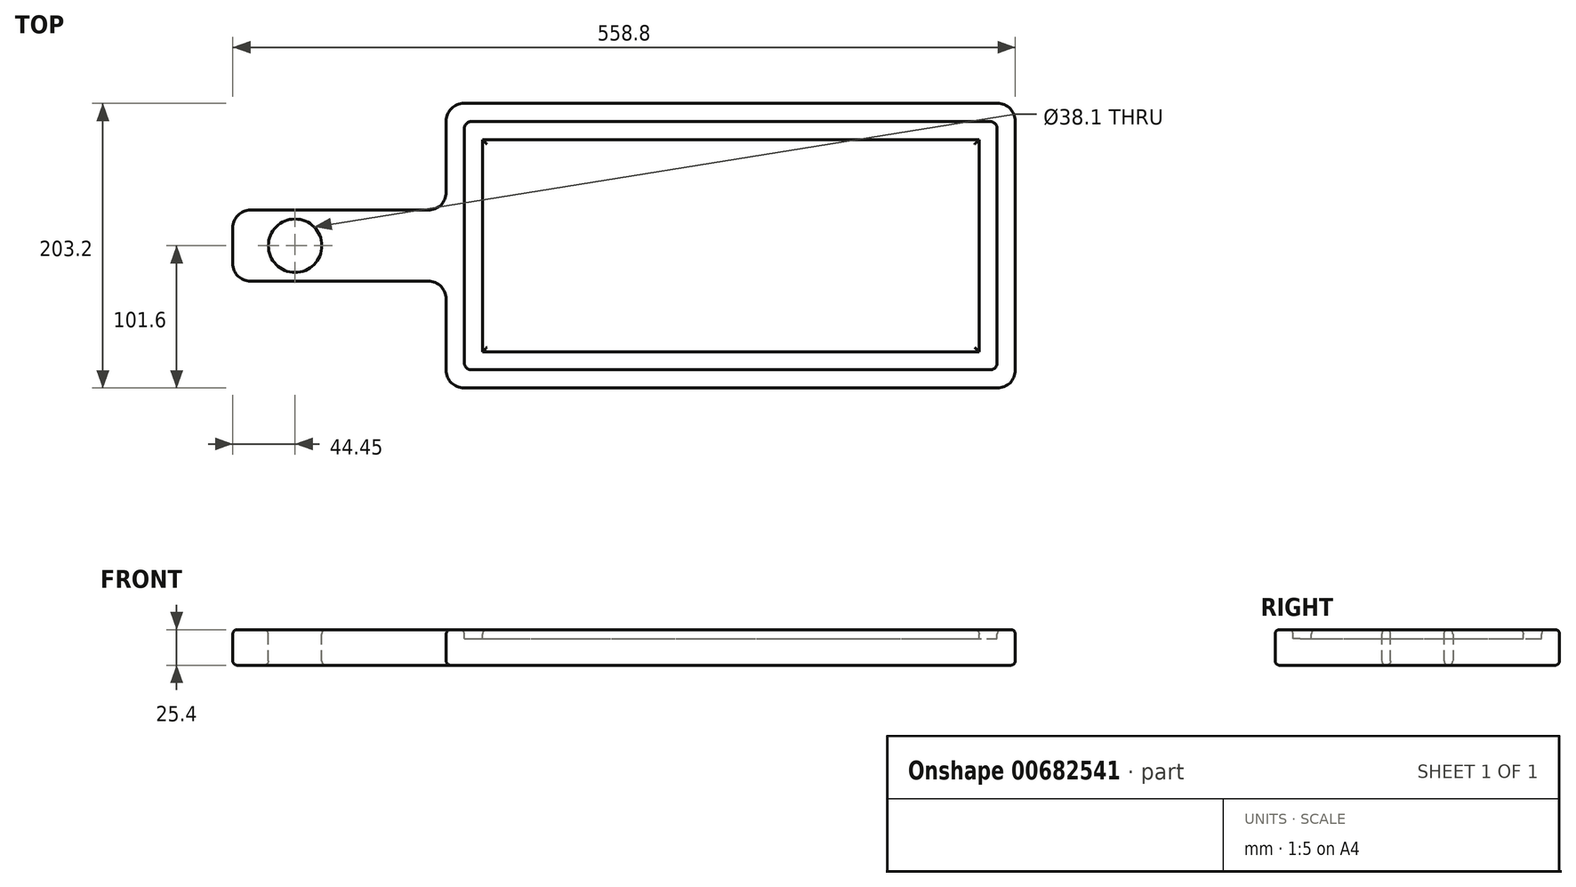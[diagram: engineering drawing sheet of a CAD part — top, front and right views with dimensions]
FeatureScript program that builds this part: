
annotation { "Feature Type Name" : "Feature", "Feature Type Description" : "" }
export const myFeature = defineFeature(function(context is Context, id is Id, definition is map)
    precondition{}
    {
        {
            var Q0;
            Q0=qCreatedBy(makeId("Top.planeOp"),FACE);
            var sketch = newSketch(context, id + "F0", { "sketchPlane" : qUnion([Q0])});
            skLineSegment(sketch, "E0.bottom", {"start": v(0, 0) * mm, "end": v(406.4, 0) * mm});
            skLineSegment(sketch, "E0.top", {"start": v(0, 203.2) * mm, "end": v(406.4, 203.2) * mm});
            skLineSegment(sketch, "E0.left", {"start": v(0, 0) * mm, "end": v(0, 203.2) * mm});
            skLineSegment(sketch, "E0.right", {"start": v(406.4, 0) * mm, "end": v(406.4, 203.2) * mm});
            skLineSegment(sketch, "E1.bottom", {"start": v(0, 127) * mm, "end": v(-152.4, 127) * mm});
            skLineSegment(sketch, "E1.top", {"start": v(0, 76.2) * mm, "end": v(-152.4, 76.2) * mm});
            skLineSegment(sketch, "E1.left", {"start": v(0, 127) * mm, "end": v(0, 76.2) * mm});
            skLineSegment(sketch, "E1.right", {"start": v(-152.4, 127) * mm, "end": v(-152.4, 76.2) * mm});
            skSolve(sketch);
        }
        {
            var Q0;
            {var subQ3=sQuery(id+"F0.wireOp",EDGE,"E0.bottom");Q0=makeQuery(id+"F0.imprint","IMPRINT",FACE,{"disambiguationData":[TD([[makeQuery(id+"F0.imprint","IMPRINT",EDGE,{"derivedFrom":subQ3}),1.0]])]});}
            var Q1;
            Q1=makeQuery(id+"F0.imprint","IMPRINT",FACE,{"disambiguationData":[TD([[makeQuery(id+"F0.imprint","IMPRINT",EDGE,{"derivedFrom":sQuery(id+"F0.wireOp",EDGE,"E1.bottom")}),1.0]])]});
            extrude(context, id + "F1", {"entities" : qUnion([Q0, Q1]), "depth" : 25.4 * mm, "offsetDistance" : 25.4 * mm});
        }
        {
            var Q0;
            Q0=makeQuery(id+"F1.opExtrude","CAP_FACE",FACE,{"disambiguationData":[OSD([sQuery(id+"F0.wireOp",EDGE,"E0.bottom"),sQuery(id+"F0.wireOp",EDGE,"E0.top"),sQuery(id+"F0.wireOp",EDGE,"E0.left"),sQuery(id+"F0.wireOp",EDGE,"E0.right"),sQuery(id+"F0.wireOp",EDGE,"E1.bottom"),sQuery(id+"F0.wireOp",EDGE,"E1.top"),sQuery(id+"F0.wireOp",EDGE,"E1.right")])],"isStart":false});
            var sketch = newSketch(context, id + "F2", { "sketchPlane" : qUnion([Q0])});
            skCircle(sketch, "E2", {"center": v(-107.95, 101.6) * mm, "radius": 19.05 * mm});
            skSolve(sketch);
        }
        {
            var Q0;
            Q0 = qSketchRegion(id + "F2", true);
            extrude(context, id + "F3", {"entities" : qUnion([Q0]), "operationType" : NewBodyOperationType.REMOVE, "oppositeDirection" : true, "depth" : 25.4 * mm, "offsetDistance" : 25.4 * mm});
        }
        {
            var Q0;
            Q0=makeQuery(id+"F1.opExtrude","CAP_FACE",FACE,{"disambiguationData":[OSD([sQuery(id+"F0.wireOp",EDGE,"E0.bottom"),sQuery(id+"F0.wireOp",EDGE,"E0.top"),sQuery(id+"F0.wireOp",EDGE,"E0.left"),sQuery(id+"F0.wireOp",EDGE,"E0.right"),sQuery(id+"F0.wireOp",EDGE,"E1.bottom"),sQuery(id+"F0.wireOp",EDGE,"E1.top"),sQuery(id+"F0.wireOp",EDGE,"E1.right")])],"isStart":false});
            var sketch = newSketch(context, id + "F4", { "sketchPlane" : qUnion([Q0])});
            skLineSegment(sketch, "E3.0", {"start": v(12.95, 12.95) * mm, "end": v(12.95, 76.2) * mm});
            skLineSegment(sketch, "E3.1", {"start": v(12.95, 127) * mm, "end": v(12.95, 190.25) * mm});
            skLineSegment(sketch, "E3.2", {"start": v(12.95, 190.25) * mm, "end": v(393.45, 190.25) * mm});
            skLineSegment(sketch, "E3.3", {"start": v(393.45, 12.95) * mm, "end": v(393.45, 190.25) * mm});
            skLineSegment(sketch, "E3.4", {"start": v(12.95, 12.95) * mm, "end": v(393.45, 12.95) * mm});
            skLineSegment(sketch, "E4", {"start": v(12.95, 127) * mm, "end": v(12.95, 76.2) * mm});
            skLineSegment(sketch, "E5.0", {"start": v(25.9, 127) * mm, "end": v(25.9, 177.3) * mm});
            skLineSegment(sketch, "E5.1", {"start": v(380.5, 25.9) * mm, "end": v(380.5, 177.3) * mm});
            skLineSegment(sketch, "E5.2", {"start": v(25.9, 25.9) * mm, "end": v(380.5, 25.9) * mm});
            skLineSegment(sketch, "E5.3", {"start": v(25.9, 177.3) * mm, "end": v(380.5, 177.3) * mm});
            skLineSegment(sketch, "E5.4", {"start": v(25.9, 25.9) * mm, "end": v(25.9, 76.2) * mm});
            skLineSegment(sketch, "E5.5", {"start": v(25.9, 127) * mm, "end": v(25.9, 76.2) * mm});
            skSolve(sketch);
        }
        {
            var Q0;
            Q0=makeQuery(id+"F4.imprint","IMPRINT",FACE,{"disambiguationData":[TD([[makeQuery(id+"F4.imprint","IMPRINT",EDGE,{"derivedFrom":sQuery(id+"F4.wireOp",EDGE,"E3.0")}),-1.0]])]});
            extrude(context, id + "F5", {"entities" : qUnion([Q0]), "operationType" : NewBodyOperationType.REMOVE, "oppositeDirection" : true, "depth" : 6.35 * mm, "offsetDistance" : 25.4 * mm});
        }
        {
            var Q0;
            Q0=makeQuery(id+"F1.opExtrude","SWEPT_EDGE",EDGE,{"disambiguationData":[OSD([sQuery(id+"F0.wireOp",EDGE,"E1.top"),sQuery(id+"F0.wireOp",EDGE,"E1.right")])]});
            var Q1;
            Q1=makeQuery(id+"F1.opExtrude","SWEPT_EDGE",EDGE,{"disambiguationData":[OSD([sQuery(id+"F0.wireOp",EDGE,"E1.bottom"),sQuery(id+"F0.wireOp",EDGE,"E1.right")])]});
            var Q2;
            Q2=makeQuery(id+"F1.opExtrude","SWEPT_EDGE",EDGE,{"disambiguationData":[OSD([sQuery(id+"F0.wireOp",EDGE,"E0.top"),sQuery(id+"F0.wireOp",EDGE,"E0.left")])]});
            var Q3;
            Q3=makeQuery(id+"F1.opExtrude","SWEPT_EDGE",EDGE,{"disambiguationData":[OSD([sQuery(id+"F0.wireOp",EDGE,"E0.bottom"),sQuery(id+"F0.wireOp",EDGE,"E0.left")])]});
            var Q4;
            Q4=makeQuery(id+"F1.opExtrude","SWEPT_EDGE",EDGE,{"disambiguationData":[OSD([sQuery(id+"F0.wireOp",EDGE,"E0.top"),sQuery(id+"F0.wireOp",EDGE,"E0.right")])]});
            var Q5;
            Q5=makeQuery(id+"F1.opExtrude","SWEPT_EDGE",EDGE,{"disambiguationData":[OSD([sQuery(id+"F0.wireOp",EDGE,"E0.bottom"),sQuery(id+"F0.wireOp",EDGE,"E0.right")])]});
            var Q6;
            Q6=makeQuery(id+"F1.opExtrude","SWEPT_EDGE",EDGE,{"disambiguationData":[OSD([sQuery(id+"F0.wireOp",EDGE,"E0.left"),sQuery(id+"F0.wireOp",EDGE,"E1.top"),sQuery(id+"F0.wireOp",EDGE,"E1.left")])]});
            var Q7;
            Q7=makeQuery(id+"F1.opExtrude","SWEPT_EDGE",EDGE,{"disambiguationData":[OSD([sQuery(id+"F0.wireOp",EDGE,"E0.left"),sQuery(id+"F0.wireOp",EDGE,"E1.bottom"),sQuery(id+"F0.wireOp",EDGE,"E1.left")])]});
            fillet(context, id + "F6", {"entities" : qUnion([Q0, Q1, Q2, Q3, Q4, Q5, Q6, Q7]), "radius" : 12.7 * mm, "tangentPropagation" : true, "allowEdgeOverflow" : false});
        }
        {
            var Q0;
            Q0=makeQuery(id+"F5.boolean.opBoolean","COPY",EDGE,{"derivedFrom":makeQuery(id+"F5.opExtrude","SWEPT_EDGE",EDGE,{"disambiguationData":[OSD([sQuery(id+"F4.wireOp",EDGE,"E3.1"),sQuery(id+"F4.wireOp",EDGE,"E3.2")])]})});
            var Q1;
            Q1=makeQuery(id+"F5.boolean.opBoolean","COPY",EDGE,{"derivedFrom":makeQuery(id+"F5.opExtrude","SWEPT_EDGE",EDGE,{"disambiguationData":[OSD([sQuery(id+"F4.wireOp",EDGE,"E3.2"),sQuery(id+"F4.wireOp",EDGE,"E3.3")])]})});
            var Q2;
            Q2=makeQuery(id+"F5.boolean.opBoolean","COPY",EDGE,{"derivedFrom":makeQuery(id+"F5.opExtrude","SWEPT_EDGE",EDGE,{"disambiguationData":[OSD([sQuery(id+"F4.wireOp",EDGE,"E3.3"),sQuery(id+"F4.wireOp",EDGE,"E3.4")])]})});
            var Q3;
            Q3=makeQuery(id+"F5.boolean.opBoolean","COPY",EDGE,{"derivedFrom":makeQuery(id+"F5.opExtrude","SWEPT_EDGE",EDGE,{"disambiguationData":[OSD([sQuery(id+"F4.wireOp",EDGE,"E3.0"),sQuery(id+"F4.wireOp",EDGE,"E3.4")])]})});
            fillet(context, id + "F7", {"entities" : qUnion([Q0, Q1, Q2, Q3]), "radius" : 5.08 * mm, "tangentPropagation" : true, "allowEdgeOverflow" : false});
        }
        {
            var Q0;
            Q0=makeQuery(id+"F5.boolean.opBoolean","SPLIT",FACE,{"disambiguationData":[TD([makeQuery(id+"F5.opExtrude","SWEPT_FACE",FACE,{"disambiguationData":[OSD([sQuery(id+"F4.wireOp",EDGE,"E5.1")])]})])],"derivedFrom":makeQuery(id+"F1.opExtrude","CAP_FACE",FACE,{"disambiguationData":[OSD([sQuery(id+"F0.wireOp",EDGE,"E0.bottom"),sQuery(id+"F0.wireOp",EDGE,"E0.top"),sQuery(id+"F0.wireOp",EDGE,"E0.left"),sQuery(id+"F0.wireOp",EDGE,"E0.right"),sQuery(id+"F0.wireOp",EDGE,"E1.bottom"),sQuery(id+"F0.wireOp",EDGE,"E1.top"),sQuery(id+"F0.wireOp",EDGE,"E1.right")])],"isStart":false})});
            var Q1;
            {var subQ0=sQuery(id+"F0.wireOp",EDGE,"E0.left");var subQ1=sQuery(id+"F0.wireOp",EDGE,"E0.top");var subQ3=sQuery(id+"F0.wireOp",EDGE,"E1.bottom");var subQ4=sQuery(id+"F0.wireOp",EDGE,"E1.right");var subQ5=sQuery(id+"F0.wireOp",EDGE,"E1.top");var subQ6=sQuery(id+"F0.wireOp",EDGE,"E0.right");var subQ7=sQuery(id+"F0.wireOp",EDGE,"E0.bottom");Q1=makeQuery(id+"F5.boolean.opBoolean","SPLIT",FACE,{"disambiguationData":[TD([makeQuery(id+"F1.opExtrude","SWEPT_FACE",FACE,{"disambiguationData":[OSD([subQ7])]})])],"derivedFrom":makeQuery(id+"F1.opExtrude","CAP_FACE",FACE,{"disambiguationData":[OSD([subQ7,subQ1,subQ0,subQ6,subQ3,subQ5,subQ4])],"isStart":false})});}
            var Q2;
            Q2=makeQuery(id+"F1.opExtrude","CAP_FACE",FACE,{"disambiguationData":[OSD([sQuery(id+"F0.wireOp",EDGE,"E0.bottom"),sQuery(id+"F0.wireOp",EDGE,"E0.top"),sQuery(id+"F0.wireOp",EDGE,"E0.left"),sQuery(id+"F0.wireOp",EDGE,"E0.right"),sQuery(id+"F0.wireOp",EDGE,"E1.bottom"),sQuery(id+"F0.wireOp",EDGE,"E1.top"),sQuery(id+"F0.wireOp",EDGE,"E1.right")])],"isStart":true});
            fillet(context, id + "F8", {"entities" : qUnion([Q0, Q1, Q2]), "radius" : 3.17 * mm, "tangentPropagation" : true, "allowEdgeOverflow" : false});
        }
    });
